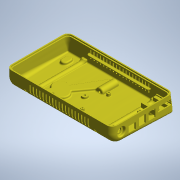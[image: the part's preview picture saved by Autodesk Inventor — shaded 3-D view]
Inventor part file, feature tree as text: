
AUTODESK INVENTOR PART (.ipt)
format: ipt  version: 2020 (Build 240168000, 168)  size: 2,651,648 bytes
history: native  units: mm
features: sketch x42, fillet x41, extrude x34, projected_geometry x10, hole x5, pattern_linear x5, plane x4, sweep x3, mirror x3, other x2
ambient origin geometry x8: Origin, YZ Plane, XZ Plane, XY Plane, X Axis, Y Axis, Z Axis, Center Point
bodies: Solid2 (feature_tree)
feature tree (149):
  extrude  "Corps"  Depth=55.5mm
  sweep  "Appui pour écran"
  fillet  "Fillet4"  Radius=2.0mm
  fillet  "Fillet5"  Radius=2.0mm
  mirror  "Mirror6"
  extrude  "Biais"  TaperAngle=0.0deg  [1 undecoded]
  extrude  "Extrusion31"  Depth=10.0mm
  fillet  "Fillet82"  Radius=10.0mm
  fillet  "Fillet55"  Radius=10.0mm
  fillet  "Fillet85"  Radius=19.0mm
  fillet  "Fillet86"  Radius=32.0mm
  other  "Work Point1"
  fillet  "Fillet87"  [1 undecoded]
  other  "Work Point2"
  fillet  "Fillet88"  Radius=2.0mm
  plane  "Work Plane10"
  sketch  "Sketch41"  dims[d445=17.0mm d456=4.0mm]
  sketch  "Sketch70"  dims[d457=2.0mm d462=10.0mm]
  sweep  "Bossage pour joint"
  sweep  "Logement pour joint"
  sketch  "Sketch72"  dims[d463=10.0mm d464=4.0mm d465=5.0mm d466=1.0mm d467=8.0mm]
  extrude  "Ebavurage 1"  Depth=1.0mm
  fillet  "Fillet89"  Radius=8.0mm
  extrude  "Bouchon 1"  Depth=10.0mm
  extrude  "Bouchon 2"  Depth=10.0mm
  extrude  "Ebavurage 2"  Depth=1.0mm
  fillet  "Fillet90"  [1 undecoded]
  fillet  "Fillet91"  Radius=0.01mm
  fillet  "Fillet92"  Radius=5.0mm
  mirror  "Mirror7"
  extrude  "Ouvertures prises"  Depth=0.4mm
  plane  "Work Plane14"
  extrude  "Bossage pour Rasp pi 1"  Depth=8.0mm
  fillet  "Fillet93"  Radius=9.0mm
  hole  "Hole8"  [1 undecoded]
  pattern_linear  "Rectangular Pattern6"  Count1=2 Spacing1=49.0mm
  extrude  "Bossage pour Rasp pi 2"  Depth=10.0mm
  fillet  "Fillet94"  Radius=10.0mm
  hole  "Hole9"  [1 undecoded]
  pattern_linear  "Rectangular Pattern7"  Spacing1=10.0mm  [1 undecoded]
  extrude  "Prise câble plat"  Depth=7.0mm
  plane  "Work Plane15"
  sketch  "Sketch83"  dims[d514=1.25mm]
  extrude  "Support cable extender"  Depth=7.0mm
  hole  "Fixation du cable extender"  [1 undecoded]
  extrude  "Bossage pour connecteur alim"  Depth=7.0mm
  extrude  "Trou pour connecteur alim"  Depth=7.0mm
  fillet  "Fillet95"  Radius=4.5mm
  fillet  "Fillet96"  Radius=20.0mm
  fillet  "Fillet97"  Radius=14.5mm
  extrude  "Logement pour pied 1"  Depth=7.0mm
  fillet  "Fillet98"  Radius=17.0mm
  fillet  "Fillet111"  Radius=3.0mm
  extrude  "Logement pour pied 2"  Depth=7.0mm
  extrude  "Logement pour pied 3"  Depth=7.0mm TaperAngle=0.0deg
  extrude  "Logement pour pied 4"  Depth=7.0mm
  extrude  "Logement pour pied 5"  Depth=1.0mm
  extrude  "Logement pour pied 6"  Depth=7.0mm
  fillet  "Fillet128"  Radius=4.0mm
  fillet  "Fillet134"  Radius=2.0mm
  fillet  "Fillet132"  Radius=4.0mm
  fillet  "Fillet135"  Radius=20.0mm
  extrude  "Axe de pied"  Depth=7.0mm
  extrude  "Logement pour pied 7"  Depth=7.0mm
  fillet  "Fillet136"  Radius=8.5mm
  extrude  "Logement pour pied 8"  Depth=7.0mm
  extrude  "Logement pour pied 9"  Depth=7.0mm
  fillet  "Fillet137"  Radius=32.0mm
  fillet  "Fillet138"  Radius=50.0mm
  fillet  "Fillet139"  Radius=0.2mm
  fillet  "Fillet140"  Radius=6.2mm
  extrude  "Dent pour pied 1"  Depth=7.0mm
  fillet  "Fillet141"  Radius=2.0mm
  fillet  "Fillet142"  Radius=2.0mm
  hole  "Trou pour vis de fixation écran"  [1 undecoded]
  extrude  "Bossage pour vis 1"  Depth=7.0mm TaperAngle=0.0deg
  extrude  "Bossage pour vis 2"  Depth=7.0mm
  extrude  "Evidement pour plaque"  Depth=7.0mm
  fillet  "Fillet144"  Radius=3.0mm
  extrude  "Ouïes"  Depth=7.0mm TaperAngle=0.0deg
  fillet  "Fillet145"  Radius=2.0mm
  pattern_linear  "Rectangular Pattern8"  Spacing1=4.0mm  [1 undecoded]
  plane  "Work Plane17"
  fillet  "Fillet148"  Radius=1.006474mm
  extrude  "Fixation par vis 1"  Depth=7.0mm
  fillet  "Fillet149"  Radius=10.0mm
  extrude  "Fixation par vis 2"  Depth=7.0mm
  extrude  "Fixation par vis 3"  Depth=7.0mm
  mirror  "Mirror8"
  hole  "Hole12"  [1 undecoded]
  extrude  "Renfort"  Depth=10.0mm
  fillet  "Fillet151"  Radius=2.0mm
  fillet  "Fillet152"  Radius=2.0mm
  fillet  "Fillet154"  Radius=2.0mm
  fillet  "Fillet155"  Radius=2.0mm
  fillet  "Fillet156"  Radius=2.0mm
  pattern_linear  "Rectangular Pattern9"  Spacing1=4.0mm  [1 undecoded]
  fillet  "Fillet157"  Radius=2.0mm
  pattern_linear  "Rectangular Pattern10"  Spacing1=1.0mm  [1 undecoded]
  fillet  "Fillet158"  Radius=1.0mm
  extrude  "Extrusion111"  Depth=7.0mm
  sketch  "Sketch1"  dims[d13=96.5mm d14=55.5mm]
  sketch  "Sketch3"  dims[d15=2.0mm d16=36.0mm d17=0.0mm d18=2.0mm d19=2.0mm]
  sketch  "3D Sketch2"
  sketch  "Sketch38"  dims[d20=2.0mm d21=0.0mm d22=0.0mm]
  sketch  "Sketch39"  dims[d23=6.0mm d24=8.0mm d310=10.0mm d311=0.0mm d313=10.0mm d314=0.0mm d316=19.0mm d328=32.0mm d329=-65.0mm d444=2.0mm]
  sketch  "Sketch73"  dims[d468=10.0mm d469=12.0mm]
  sketch  "Sketch74"  dims[d470=10.0mm d471=2.5mm]
  projected_geometry  "Projected Loop2"
  sketch  "Sketch75"  dims[d472=2.0mm d473=1.0mm d479=0.0mm d480=0.0mm d481=0.01mm d482=0.0mm d483=5.0mm]
  sketch  "Sketch76"  dims[d484=0.0mm d485=0.0mm d486=0.4mm]
  sketch  "Sketch77"  dims[d487=30.0deg d488=8.0mm]
  projected_geometry  "Projected Loop3"
  projected_geometry  "Projected Loop4"
  sketch  "Sketch78"  dims[d489=8.0mm d490=2.0mm d491=5.0mm d492=9.0mm]
  sketch  "Sketch79"  dims[d493=1.0mm d494=0.0mm d495=1.0mm d496=0.0mm]
  sketch  "Sketch80"  dims[d497=6.0mm]
  sketch  "Sketch82"  dims[d502=12.2mm d503=12.2mm d504=14.0mm d505=8.0mm d506=18.2mm d512=2.0mm d513=0.0mm]
  projected_geometry  "Projected Loop5"
  sketch  "Sketch84"  dims[d515=84.0mm]
  sketch  "Sketch85"  dims[d516=14.888889mm]
  sketch  "Sketch86"  dims[d517=18.0mm]
  sketch  "Sketch87"  dims[d518=11.0mm]
  sketch  "Sketch88"  dims[d519=21.0mm]
  sketch  "Sketch111"  dims[d520=1.0mm]
  sketch  "Sketch112"  dims[d521=1.0mm]
  sketch  "Sketch113"  dims[d522=1.0mm]
  sketch  "Sketch114"  dims[d523=5.0mm]
  sketch  "Sketch115"  dims[d524=35.339mm]
  sketch  "Sketch116"  dims[d525=27.872mm]
  sketch  "Sketch117"  dims[d526=6.0mm]
  sketch  "Sketch118"  dims[d527=10.0mm d528=0.0mm]
  projected_geometry  "Projected Loop7"
  sketch  "Sketch119"  dims[d529=1.0mm]
  sketch  "Sketch120"  dims[d530=2.5mm d531=6.0mm d532=4.0mm d533=2.0mm d534=90.0deg d535=5.0mm d536=0.0mm d543=20.0mm d545=49.0mm]
  sketch  "Sketch122"  dims[d546=6.0mm d547=58.0mm d548=10.0mm d549=0.0mm]
  sketch  "Sketch123"  dims[d550=1.0mm]
  sketch  "Sketch124"  dims[d551=2.5mm d552=6.0mm d553=4.0mm d554=2.0mm d555=90.0deg d556=5.0mm d557=0.0mm d558=20.0mm d560=49.0mm]
  sketch  "Sketch125"  dims[d565=25.4mm]
  sketch  "Sketch127"  dims[d566=22.5mm]
  sketch  "Sketch128"  dims[d567=7.0mm]
  sketch  "Sketch129"  dims[d568=1.8mm]
  sketch  "Sketch130"  dims[d569=5.0mm d570=0.0mm]
  sketch  "Sketch131"  dims[d572=14.9mm d573=10.0mm d576=6.0mm d577=2.0mm d579=5.0mm d580=0.0mm d581=7.0mm d582=7.0mm d583=4.5mm d584=20.0mm d585=1.5mm d586=6.0mm d587=4.0mm d588=2.0mm d589=90.0deg d590=5.0mm d591=0.0mm d594=14.5mm d595=39.5mm d596=17.0mm d597=3.0mm d598=0.0mm d601=8.0mm d602=2.0mm d603=0.0mm d604=2.0mm d605=1.0mm d606=2.0mm d608=4.0mm d615=2.0mm d616=0.0mm d630=4.0mm d632=20.0mm d660=46.0mm d661=8.0mm d662=8.5mm d663=2.0mm d694=6.0mm d695=32.0mm d696=50.0mm d722=0.2mm d729=6.2mm d730=0.0mm d732=2.0mm d734=2.0mm d735=0.0mm d736=2.0mm d737=0.0mm d740=2.0mm d741=0.0mm d742=2.0mm d743=0.0mm d744=6.2mm d748=4.2mm d750=3.0mm d751=30.0mm d752=3.0mm d753=0.0mm d754=0.0mm d755=2.0mm d756=4.0mm d757=1.006474mm d758=0.503237mm d759=10.0mm d760=20.0mm d761=35.0mm d762=30.0mm d763=0.0mm d764=10.0mm d765=2.0mm d766=0.0mm d767=2.0mm d768=2.0mm d769=2.0mm d770=0.0mm d771=2.0mm d772=4.0mm d773=2.0mm d774=1.0mm d775=1.0mm d776=4.0mm d777=0.2mm d778=0.0mm d779=0.2mm d780=0.2mm d781=1.5mm d782=7.0mm d783=6.0mm d784=4.0mm d785=2.0mm d786=90.0deg d787=8.0mm d788=20.594885mm d795=2.525mm d796=1.5mm d797=1.5mm d798=0.0mm d799=3.2mm d800=2.0mm d801=0.0mm d802=20.0mm d803=40.0mm d806=0.4mm d807=0.0mm d808=2.0mm d809=25.0mm d810=6.0mm d811=15.0mm d812=2.0mm d813=0.0mm d814=1.0mm d815=190.0mm d817=6.0mm d818=5.0mm d827=1.0mm d828=0.0mm d829=0.0mm d830=8.4mm d831=12.0mm d832=75.0mm d833=40.0mm d834=6.0mm d835=7.0mm d836=0.0mm d837=2.0mm d838=4.0mm d839=2.5mm d840=5.0mm d841=0.0mm d842=3.0mm d843=0.0mm d845=14.0mm d846=18.75mm d847=12.5mm d848=3.8mm d849=11.2mm d850=3.8mm d851=5.5mm d852=21.0mm d853=1.5mm d854=6.0mm d855=4.0mm d856=2.0mm d857=90.0deg d858=8.0mm d859=20.594885mm d860=2.0mm d861=5.0mm d862=115.0mm d863=0.0mm d864=4.0mm d865=0.5mm d867=1.0mm d868=0.9mm d869=5.0mm d870=1.0mm d871=180.0mm d873=6.0mm d874=1.0mm d875=180.0mm d877=6.0mm d878=1.0mm d879=7.0mm d880=17.6mm d881=0.0mm]
  projected_geometry  "Project Cut Edges9"
  projected_geometry  "Project Cut Edges10"
  projected_geometry  "Project Cut Edges24"
  projected_geometry  "Project Cut Edges25"
  projected_geometry  "Project Cut Edges26"
note: 12 required parameter values undecoded (feature->parameter linkage not recoverable at this tier; creation-order binding heuristic only, values carry confidence <= 0.55)
